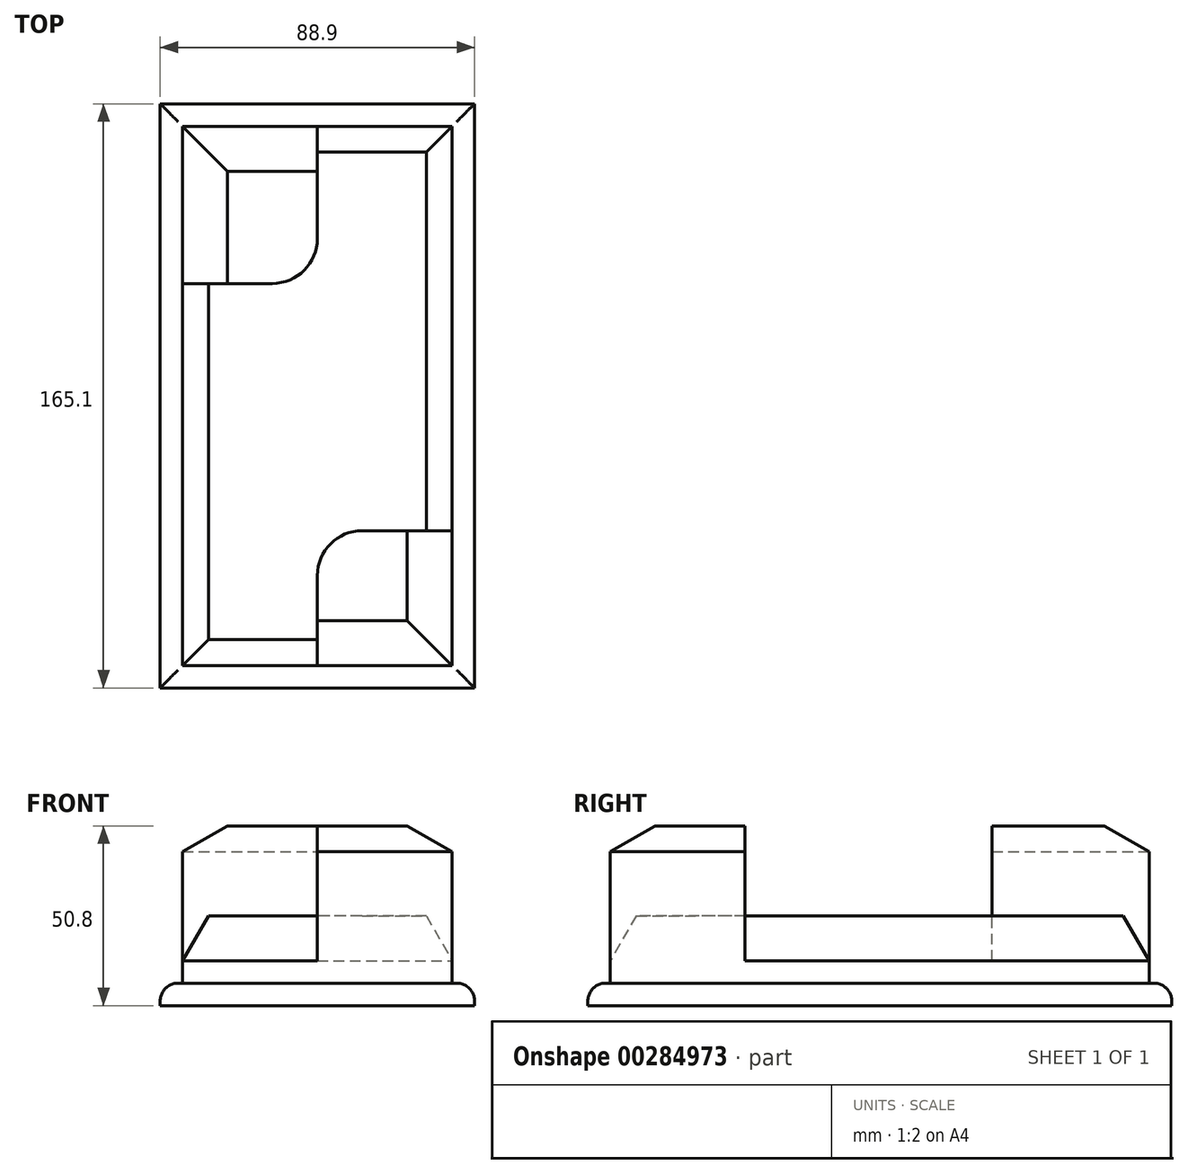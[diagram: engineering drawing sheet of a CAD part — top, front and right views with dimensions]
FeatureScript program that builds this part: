
annotation { "Feature Type Name" : "Feature", "Feature Type Description" : "" }
export const myFeature = defineFeature(function(context is Context, id is Id, definition is map)
    precondition{}
    {
        {
            var Q0;
            Q0=qCreatedBy(makeId("Top.planeOp"),FACE);
            var sketch = newSketch(context, id + "F0", { "sketchPlane" : qUnion([Q0])});
            skLineSegment(sketch, "E0.bottom", {"start": v(-38.82, 106.91) * mm, "end": v(50.08, 106.91) * mm});
            skLineSegment(sketch, "E0.top", {"start": v(-38.82, -58.19) * mm, "end": v(50.08, -58.19) * mm});
            skLineSegment(sketch, "E0.left", {"start": v(-38.82, 106.91) * mm, "end": v(-38.82, -58.19) * mm});
            skLineSegment(sketch, "E0.right", {"start": v(50.08, 106.91) * mm, "end": v(50.08, -58.19) * mm});
            skLineSegment(sketch, "E1.bottom", {"start": v(-32.47, 100.56) * mm, "end": v(43.73, 100.56) * mm});
            skLineSegment(sketch, "E1.top", {"start": v(-32.47, -51.84) * mm, "end": v(43.73, -51.84) * mm});
            skLineSegment(sketch, "E1.left", {"start": v(-32.47, 100.56) * mm, "end": v(-32.47, -51.84) * mm});
            skLineSegment(sketch, "E1.right", {"start": v(43.73, 100.56) * mm, "end": v(43.73, -51.84) * mm});
            skLineSegment(sketch, "E2", {"start": v(-32.47, 56.11) * mm, "end": v(-7.07, 56.11) * mm});
            skLineSegment(sketch, "E3", {"start": v(5.63, 68.81) * mm, "end": v(5.63, 100.56) * mm});
            skLineSegment(sketch, "E4", {"start": v(5.63, -51.84) * mm, "end": v(5.63, -26.44) * mm});
            skLineSegment(sketch, "E5", {"start": v(18.33, -13.74) * mm, "end": v(43.73, -13.74) * mm});
            skPoint(sketch, "E6.visualSharp", {"position": v(5.63, 56.11) * mm});
            skArc(sketch, "E6.filletArc", {"start": v(-7.07, 56.11) * mm, "mid": v(1.91, 59.83) * mm, "end": v(5.63, 68.81) * mm});
            skPoint(sketch, "E7.visualSharp", {"position": v(5.63, -13.74) * mm});
            skArc(sketch, "E7.filletArc", {"start": v(18.33, -13.74) * mm, "mid": v(9.35, -17.46) * mm, "end": v(5.63, -26.44) * mm});
            skSolve(sketch);
        }
        {
            var Q0;
            Q0=makeQuery(id+"F0.imprint","IMPRINT",FACE,{"disambiguationData":[TD([[makeQuery(id+"F0.imprint","IMPRINT",EDGE,{"derivedFrom":sQuery(id+"F0.wireOp",EDGE,"E0.bottom")}),-1.0]])]});
            extrude(context, id + "F1", {"entities" : qUnion([Q0]), "depth" : 6.35 * mm});
        }
        {
            var Q0;
            {var subQ3=sQuery(id+"F0.wireOp",EDGE,"E2");Q0=makeQuery(id+"F0.imprint","IMPRINT",FACE,{"disambiguationData":[TD([[makeQuery(id+"F0.imprint","IMPRINT",EDGE,{"derivedFrom":subQ3}),-1.0]])]});}
            extrude(context, id + "F2", {"entities" : qUnion([Q0]), "operationType" : NewBodyOperationType.ADD, "depth" : 25.4 * mm});
        }
        {
            var Q0;
            {var subQ1=sQuery(id+"F0.wireOp",EDGE,"E4");Q0=makeQuery(id+"F0.imprint","IMPRINT",FACE,{"disambiguationData":[TD([[makeQuery(id+"F0.imprint","IMPRINT",EDGE,{"derivedFrom":subQ1}),-1.0]])]});}
            var Q1;
            {var subQ0=sQuery(id+"F0.wireOp",EDGE,"E2");Q1=makeQuery(id+"F0.imprint","IMPRINT",FACE,{"disambiguationData":[TD([[makeQuery(id+"F0.imprint","IMPRINT",EDGE,{"derivedFrom":subQ0}),1.0]])]});}
            extrude(context, id + "F3", {"entities" : qUnion([Q0, Q1]), "operationType" : NewBodyOperationType.ADD, "depth" : 50.8 * mm});
        }
        {
            var Q0;
            Q0=makeQuery(id+"F1.opExtrude","CAP_EDGE",EDGE,{"disambiguationData":[OSD([sQuery(id+"F0.wireOp",EDGE,"E0.left")])],"isStart":false});
            var Q1;
            Q1=makeQuery(id+"F1.opExtrude","CAP_EDGE",EDGE,{"disambiguationData":[OSD([sQuery(id+"F0.wireOp",EDGE,"E0.top")])],"isStart":false});
            var Q2;
            Q2=makeQuery(id+"F1.opExtrude","CAP_EDGE",EDGE,{"disambiguationData":[OSD([sQuery(id+"F0.wireOp",EDGE,"E0.right")])],"isStart":false});
            var Q3;
            Q3=makeQuery(id+"F1.opExtrude","CAP_EDGE",EDGE,{"disambiguationData":[OSD([sQuery(id+"F0.wireOp",EDGE,"E0.bottom")])],"isStart":false});
            fillet(context, id + "F4", {"entities" : qUnion([Q0, Q1, Q2, Q3]), "radius" : 5.08 * mm, "tangentPropagation" : true, "allowEdgeOverflow" : false});
        }
        {
            var Q0;
            Q0=makeQuery(id+"F2.opExtrude","CAP_EDGE",EDGE,{"disambiguationData":[OSD([sQuery(id+"F0.wireOp",EDGE,"E1.right")])],"isStart":false});
            var Q1;
            Q1=makeQuery(id+"F2.opExtrude","CAP_EDGE",EDGE,{"disambiguationData":[OSD([sQuery(id+"F0.wireOp",EDGE,"E1.bottom")])],"isStart":false});
            var Q2;
            Q2=makeQuery(id+"F2.opExtrude","CAP_EDGE",EDGE,{"disambiguationData":[OSD([sQuery(id+"F0.wireOp",EDGE,"E1.left")])],"isStart":false});
            var Q3;
            Q3=makeQuery(id+"F2.opExtrude","CAP_EDGE",EDGE,{"disambiguationData":[OSD([sQuery(id+"F0.wireOp",EDGE,"E1.top")])],"isStart":false});
            chamfer(context, id + "F5", {"entities" : qUnion([Q0, Q1, Q2, Q3]), "chamferType" : ChamferType.OFFSET_ANGLE, "width" : 12.7 * mm, "oppositeDirection" : false, "angle" : 30 * degree, "tangentPropagation" : true});
        }
        {
            var Q0;
            Q0=makeQuery(id+"F3.opExtrude","CAP_EDGE",EDGE,{"disambiguationData":[OSD([sQuery(id+"F0.wireOp",EDGE,"E1.top")])],"isStart":false});
            var Q1;
            Q1=makeQuery(id+"F3.opExtrude","CAP_EDGE",EDGE,{"disambiguationData":[OSD([sQuery(id+"F0.wireOp",EDGE,"E1.right")])],"isStart":false});
            chamfer(context, id + "F6", {"entities" : qUnion([Q0, Q1]), "chamferType" : ChamferType.OFFSET_ANGLE, "width" : 12.7 * mm, "oppositeDirection" : false, "angle" : 30 * degree, "tangentPropagation" : true});
        }
        {
            var Q0;
            Q0=makeQuery(id+"F3.opExtrude","CAP_EDGE",EDGE,{"disambiguationData":[OSD([sQuery(id+"F0.wireOp",EDGE,"E1.left")])],"isStart":false});
            var Q1;
            Q1=makeQuery(id+"F3.opExtrude","CAP_EDGE",EDGE,{"disambiguationData":[OSD([sQuery(id+"F0.wireOp",EDGE,"E1.bottom")])],"isStart":false});
            chamfer(context, id + "F7", {"entities" : qUnion([Q0, Q1]), "chamferType" : ChamferType.OFFSET_ANGLE, "width" : 12.7 * mm, "oppositeDirection" : false, "angle" : 30 * degree, "tangentPropagation" : true});
        }
    });
